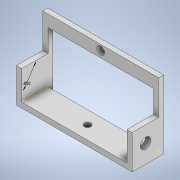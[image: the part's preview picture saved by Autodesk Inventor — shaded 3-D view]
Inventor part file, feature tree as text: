
AUTODESK INVENTOR PART (.ipt)
format: ipt  version: 2021.2 (Build 252289000, 289)  size: 293,376 bytes
history: native  units: in
note: dims shown in document units (in); Inventor stores cm internally (conversion verified against a paired STEP export)
features: sketch x28, extrude x21
ambient origin geometry x8: Origin, YZ Plane, XZ Plane, XY Plane, X Axis, Y Axis, Z Axis, Center Point
bodies: Solid1 (feature_tree)
feature tree (49):
  extrude  "Extrusion1"  Depth=4.0in
  extrude  "Extrusion2"  Depth=0.2in
  sketch  "Sketch3"  dims[d4=0.2in d5=0.2in]
  extrude  "Extrusion3"  Depth=0.2in
  extrude  "Extrusion4"  Depth=2.0in
  sketch  "Sketch7"  dims[d11=0.1875in d12=0.0in d13=0.125in d14=0.0in]
  extrude  "Extrusion6"  Depth=0.2in
  sketch  "Sketch9"  dims[d21=0.3in d22=0.0in d23=0.0125in d24=0.0in]
  extrude  "Extrusion7"  Depth=0.125in TaperAngle=0.0deg
  sketch  "Sketch10"  dims[d25=0.2in d26=2.0in d27=0.0in]
  sketch  "Sketch11"  dims[d28=0.2in d29=2.0in d30=0.0in]
  extrude  "Extrusion8"  Depth=0.4in
  extrude  "Extrusion9"  Depth=0.0125in TaperAngle=0.0deg
  extrude  "Extrusion10"  Depth=2.0in TaperAngle=0.0deg
  extrude  "Extrusion11"  Depth=2.0in TaperAngle=0.0deg
  extrude  "Extrusion12"  Depth=0.188in TaperAngle=0.0deg
  sketch  "Sketch17"  dims[d48=0.4in d49=0.5in d50=0.0in]
  sketch  "Sketch18"  dims[d51=0.5in d52=0.0in d53=4.0in]
  extrude  "Extrusion13"  Depth=0.188in
  extrude  "Extrusion14"  Depth=0.3755in TaperAngle=0.0deg
  extrude  "Extrusion15"  Depth=0.5in TaperAngle=0.0deg
  extrude  "Extrusion16"  Depth=0.5in TaperAngle=0.0deg
  extrude  "Extrusion17"  Depth=0.5in TaperAngle=0.0deg
  extrude  "Extrusion18"  Depth=4.0in
  extrude  "Extrusion19"  Depth=0.5in TaperAngle=0.0deg
  extrude  "Extrusion20"  Depth=0.3in
  extrude  "Extrusion21"  Depth=0.4in TaperAngle=0.0deg
  sketch  "Sketch28"
  extrude  "Extrusion22"  [1 undecoded]
  sketch  "Sketch1"  dims[d0=1.0in d1=4.0in]
  sketch  "Sketch2"  dims[d2=1.0in d3=0.2in]
  sketch  "Sketch4"  dims[d6=1.0in d7=0.0in d8=2.0in]
  sketch  "Sketch5"  dims[d9=0.2in d10=0.2in]
  sketch  "Sketch8"  dims[d15=0.1875in d16=0.0in d20=0.4in]
  sketch  "Sketch12"  dims[d31=1.0in d32=0.0in d33=0.188in d34=0.0in]
  sketch  "Sketch13"  dims[d35=0.188in d36=0.0in d37=0.85in]
  sketch  "Sketch14"  dims[d38=0.25in d39=0.3755in d40=0.0in]
  sketch  "Sketch15"  dims[d41=0.5in d42=0.0in d43=0.5in d44=0.0in]
  sketch  "Sketch16"  dims[d45=0.4in d46=0.5in d47=0.0in]
  sketch  "Sketch19"  dims[d54=0.3in d55=0.5in d56=0.0in]
  sketch  "Sketch20"  dims[d57=0.4in d58=0.0in d60=0.3in]
  sketch  "Sketch21"  dims[d61=0.4in d62=0.0in d63=0.4in d64=0.0in]
  sketch  "Sketch22"
  sketch  "Sketch23"
  sketch  "Sketch24"
  sketch  "Sketch25"
  sketch  "Sketch26"
  sketch  "Sketch27"
  sketch  "Sketch29"
note: 1 required parameter value undecoded (feature->parameter linkage not recoverable at this tier; creation-order binding heuristic only, values carry confidence <= 0.55)
